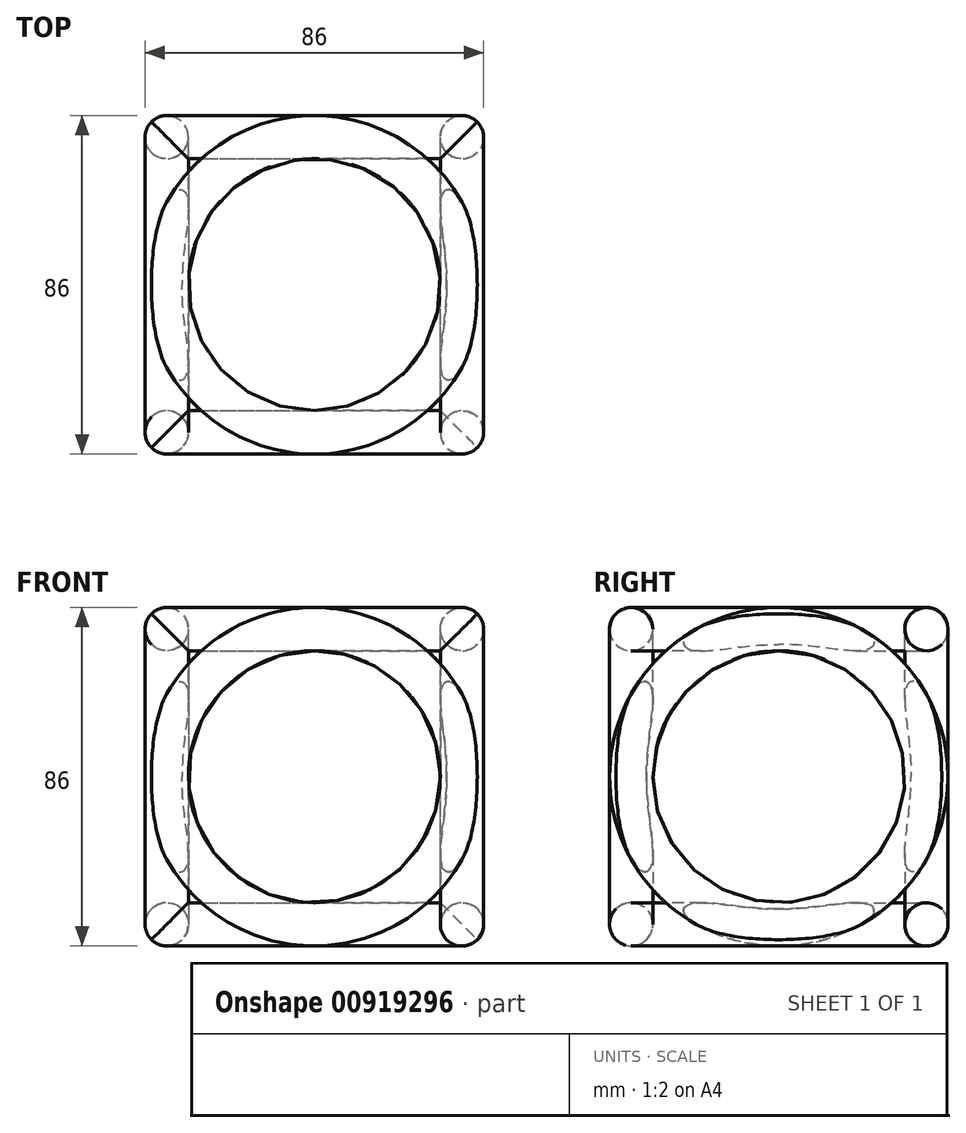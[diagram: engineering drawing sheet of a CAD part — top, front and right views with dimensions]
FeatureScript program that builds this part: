
annotation { "Feature Type Name" : "Feature", "Feature Type Description" : "" }
export const myFeature = defineFeature(function(context is Context, id is Id, definition is map)
    precondition{}
    {
        {
            var Q0;
            Q0=qCreatedBy(makeId("Top.planeOp"),FACE);
            var sketch = newSketch(context, id + "F0", { "sketchPlane" : qUnion([Q0])});
            skCircle(sketch, "E0", {"center": v(0, 0) * mm, "radius": 32 * mm});
            skCircle(sketch, "E1", {"center": v(0, 0) * mm, "radius": 53.03 * mm, "construction": true});
            skLineSegment(sketch, "E2.bottom", {"start": v(43, 43) * mm, "end": v(-43, 43) * mm});
            skLineSegment(sketch, "E2.top", {"start": v(43, -43) * mm, "end": v(-43, -43) * mm});
            skLineSegment(sketch, "E2.left", {"start": v(43, 43) * mm, "end": v(43, -43) * mm});
            skLineSegment(sketch, "E2.right", {"start": v(-43, 43) * mm, "end": v(-43, -43) * mm});
            skCircle(sketch, "E3", {"center": v(-37.5, 37.5) * mm, "radius": 5.5 * mm});
            skCircle(sketch, "E4", {"center": v(-37.5, -37.5) * mm, "radius": 5.5 * mm});
            skCircle(sketch, "E5", {"center": v(37.5, -37.5) * mm, "radius": 5.5 * mm});
            skCircle(sketch, "E6", {"center": v(37.5, 37.5) * mm, "radius": 5.5 * mm});
            skLineSegment(sketch, "E7", {"start": v(37.5, 37.5) * mm, "end": v(-37.5, 37.5) * mm, "construction": true});
            skLineSegment(sketch, "E8", {"start": v(-37.5, 37.5) * mm, "end": v(-37.5, -37.5) * mm, "construction": true});
            skLineSegment(sketch, "E9", {"start": v(37.5, -37.5) * mm, "end": v(-37.5, -37.5) * mm, "construction": true});
            skLineSegment(sketch, "E10", {"start": v(37.5, -37.5) * mm, "end": v(37.5, 37.5) * mm, "construction": true});
            skLineSegment(sketch, "E11", {"start": v(-69.35, 0) * mm, "end": v(69.97, 0) * mm, "construction": true});
            skPoint(sketch, "E11.endSnap0", {"position": v(37.5, 0) * mm});
            skSolve(sketch);
        }
        {
            var Q0;
            Q0=sQuery(id+"F0.wireOp",EDGE,"E7");
            cPlane(context, id + "F1", {"entities" : qUnion([Q0]), "cplaneType" : CPlaneType.LINE_ANGLE, "offset" : 25 * mm, "angle" : 0 * degree, "oppositeDirection" : true, "width" : 150 * mm, "height" : 150 * mm});
        }
        {
            var Q0;
            Q0=qCreatedBy(id+"F1.planeOp",FACE);
            var sketch = newSketch(context, id + "F2", { "sketchPlane" : qUnion([Q0])});
            skCircle(sketch, "E12", {"center": v(0, 0) * mm, "radius": 43 * mm});
            skSolve(sketch);
        }
        {
            var Q0;
            {var subQ0=sQuery(id+"F0.wireOp",EDGE,"E6");var subQ1=makeQuery(id+"F0.imprint","INTERSECT",VERTEX,{"derivedFrom":[sQuery(id+"F0.wireOp",EDGE,"E2.bottom"),subQ0]});Q0=makeQuery(id+"F0.imprint","IMPRINT",FACE,{"disambiguationData":[TD([[makeQuery(id+"F0.imprint","IMPRINT",EDGE,{"disambiguationData":[TD([[subQ1,1.0]])],"derivedFrom":subQ0}),1.0]])]});}
            var Q1;
            Q1=sQuery(id+"F2.wireOp",EDGE,"E12");
            sweep(context, id + "F3", {"profiles" : qUnion([Q0]), "path" : qUnion([Q1])});
        }
        {
            var Q0;
            Q0=sQuery(id+"F0.wireOp",EDGE,"E8");
            cPlane(context, id + "F4", {"entities" : qUnion([Q0]), "cplaneType" : CPlaneType.LINE_ANGLE, "offset" : 25 * mm, "angle" : 90 * degree, "width" : 150 * mm, "height" : 150 * mm});
        }
        {
            var Q0;
            Q0=qCreatedBy(id+"F4.planeOp",FACE);
            var sketch = newSketch(context, id + "F5", { "sketchPlane" : qUnion([Q0])});
            skCircle(sketch, "E13", {"center": v(0, 0) * mm, "radius": 43 * mm});
            skSolve(sketch);
        }
        {
            var Q0;
            {var subQ0=sQuery(id+"F0.wireOp",EDGE,"E4");var subQ1=makeQuery(id+"F0.imprint","INTERSECT",VERTEX,{"derivedFrom":[sQuery(id+"F0.wireOp",EDGE,"E2.top"),subQ0]});Q0=makeQuery(id+"F0.imprint","IMPRINT",FACE,{"disambiguationData":[TD([[makeQuery(id+"F0.imprint","IMPRINT",EDGE,{"disambiguationData":[TD([[subQ1,1.0]])],"derivedFrom":subQ0}),1.0]])]});}
            var Q1;
            Q1=sQuery(id+"F5.wireOp",EDGE,"E13");
            sweep(context, id + "F6", {"operationType" : NewBodyOperationType.ADD, "profiles" : qUnion([Q0]), "path" : qUnion([Q1])});
        }
        {
            var Q0;
            Q0=sQuery(id+"F0.wireOp",EDGE,"E9");
            cPlane(context, id + "F7", {"entities" : qUnion([Q0]), "cplaneType" : CPlaneType.LINE_ANGLE, "offset" : 25 * mm, "angle" : 0 * degree, "width" : 150 * mm, "height" : 150 * mm});
        }
        {
            var Q0;
            Q0=sQuery(id+"F0.wireOp",EDGE,"E10");
            cPlane(context, id + "F8", {"entities" : qUnion([Q0]), "cplaneType" : CPlaneType.LINE_ANGLE, "offset" : 25 * mm, "angle" : 90 * degree, "width" : 150 * mm, "height" : 150 * mm});
        }
        {
            var Q0;
            Q0=qCreatedBy(id+"F7.planeOp",FACE);
            var sketch = newSketch(context, id + "F9", { "sketchPlane" : qUnion([Q0])});
            skCircle(sketch, "E14", {"center": v(0, 0) * mm, "radius": 43 * mm});
            skSolve(sketch);
        }
        {
            var Q0;
            {var subQ0=sQuery(id+"F0.wireOp",EDGE,"E5");var subQ1=makeQuery(id+"F0.imprint","INTERSECT",VERTEX,{"derivedFrom":[sQuery(id+"F0.wireOp",EDGE,"E2.top"),subQ0]});Q0=makeQuery(id+"F0.imprint","IMPRINT",FACE,{"disambiguationData":[TD([[makeQuery(id+"F0.imprint","IMPRINT",EDGE,{"disambiguationData":[TD([[subQ1,1.0]])],"derivedFrom":subQ0}),1.0]])]});}
            var Q1;
            Q1=sQuery(id+"F9.wireOp",EDGE,"E14");
            sweep(context, id + "F10", {"operationType" : NewBodyOperationType.ADD, "profiles" : qUnion([Q0]), "path" : qUnion([Q1])});
        }
        {
            var Q0;
            Q0=qCreatedBy(id+"F8.planeOp",FACE);
            var sketch = newSketch(context, id + "F11", { "sketchPlane" : qUnion([Q0])});
            skCircle(sketch, "E15", {"center": v(0, 0) * mm, "radius": 43 * mm});
            skSolve(sketch);
        }
        {
            var Q0;
            {var subQ0=sQuery(id+"F0.wireOp",EDGE,"E5");var subQ1=makeQuery(id+"F0.imprint","INTERSECT",VERTEX,{"derivedFrom":[sQuery(id+"F0.wireOp",EDGE,"E2.top"),subQ0]});Q0=makeQuery(id+"F0.imprint","IMPRINT",FACE,{"disambiguationData":[TD([[makeQuery(id+"F0.imprint","IMPRINT",EDGE,{"disambiguationData":[TD([[subQ1,1.0]])],"derivedFrom":subQ0}),1.0]])]});}
            var Q1;
            Q1=sQuery(id+"F11.wireOp",EDGE,"E15");
            sweep(context, id + "F12", {"operationType" : NewBodyOperationType.ADD, "profiles" : qUnion([Q0]), "path" : qUnion([Q1])});
        }
        {
            var Q0;
            Q0=makeQuery(id+"F3.opSweep","SWEPT_BODY",BODY,{"disambiguationData":[OSD([sQuery(id+"F0.wireOp",EDGE,"E6"),sQuery(id+"F2.wireOp",EDGE,"E12")])]});
            var Q1;
            Q1=sQuery(id+"F0.wireOp",EDGE,"E11");
            transform(context, id + "F13", {"entities" : qUnion([Q0]), "transformType" : TransformType.ROTATION, "transformAxis" : qUnion([Q1]), "angle" : 90 * degree, "makeCopy" : true});
        }
    });
